# Revit family: PRD_AR_PprTwlDspnsrs_STRATOSPaperTowelDispenser_STRX637_STRX635B
name_source: partatom
category: Specialty Equipment
revit_build: Autodesk Revit 2018 (Build: 20190510_1515(x64)
units: mm (PartAtom-declared; Revit-internal decimal feet)

## family parameters
Cut with Voids When Loaded = No
Host = Face
OmniClass Number = 23.40.20.21.17
OmniClass Title = Paper Towel Dispensers, Disposal Units
Part Type = Normal
Room Calculation Point = No
Round Connector Dimension = Use Diameter
Shared = No

## types (2) — shared parameters
AssetType = Fixed
Category = Pr_40_70_22_62, Paper Towel Dispensers
Default Elevation = 900 mm  [stored 2.95276 ft]
DispenserMaterial = PRD_AR_StainlessSteel_SatinFinished
DurationUnit = year
Features = stainless steel, surface satin finished
FillingQuantity = 1
FillingQuantityUom = Rolls
Finish = satin finished
IfcExportAs = IfcFurnitureType
IfcExportType = USERDEFINED
IntegralAccessories = incl. stainless steel screws and dowels
IsBuiltIn = TRUE
Lock = Key-lock
MainColor = stainless steel
Manufacturer = KWC Group AG
ManufacturerName = KWC Group AG
ManufacturerURL = www.kwc.com
Material = stainless steel
MaterialCode = 1.4301
MaterialThickness = 1.50 mm
NBSDescription = Paper towel dispensers
NBSReference = 45-35-72/344
ProductInformation = https://pim.kwc.com
Style = dispenser
SurfaceTreatment = InoxPlus (anti fingerprint)
TypeOfConsumable = Paper roll
TypeOfFixing = Screw
TypeOfMounting = Wall mounting
TypeOfOperation = Manual operation
URL = www.kwc.com
Uniclass2015Code = Pr_40_70_22_62
Uniclass2015Title = Paper towel dispensers
Uniclass2015Version = Products v1.10
Version = 1
WarrantyDurationUnit = year

## per-type parameters (varying)
| type | BIMObjectName | Description | GrossWeight | MaximumDepthDiameterOfConsumable | MaximumWidthOfConsumable | ModelNumber | Name | NetWeight | NominalDepth | NominalHeight | NominalWidth | Size |
| STRX637 | PRD_AR_PaperTowelDispensers_STRATOSPaperTowelDispenser_STRX637 | Manual paper towel dispenser for wall mounting, stainless steel, surface satin finished, front with InoxPlus surface refinement for the reduction of finger marks and better cleaning characteristics (easy to clean), material thickness 1.5 mm, curved front with inspection window, cylinder lock with KWC standard key, capacity 1 paper roll, paper comes automatically out to pull with hand, maintenance free mechanic, electrical connection or batteries are not required, easypaper roll change mechanism, for rolls with max. width 205 mm and max. diameter 200 mm, paper length is not adjustable - one length 260 mm, includes stainless steel screws and dowels. | 7.77 kg | 200.00 mm | 205.00 mm | 2000110533 | Paper Towel Dispenser STRX637 | 7.16 kg | 227 mm  [stored 0.744751 ft] | 385 mm  [stored 1.26312 ft] | 294 mm  [stored 0.964567 ft] | 294 x 385 x 227 mm |
| STRX635B | PRD_AR_PaperTowelDispensers_STRATOSPaperTowelDispenser_STRX635B | Centerfeed paper roll box for wall mounting, stainless steel, surface satin finished, front with InoxPlus surface refinement for the reduction of finger marks and better cleaning characteristics (easy to clean), material thickness 1.5 mm, curved front cover, cylinder lock with KWC standard key, for paper rolls with max. Ø 190 mm and max. height of 250 mm, only for centerfeed paper rolls, integrated w/ stainless steel tear- off edge and strain relief avoiding paper tear-off within casing, includes stainless steel screws and dowels. | 5.32 kg | 190.00 mm | 250.00 mm | 2030025051 | Paper Towel Dispenser STRX635B | 4.70 kg | 240 mm  [stored 0.787402 ft] | 343 mm  [stored 1.12533 ft] | 205 mm  [stored 0.672572 ft] | 205 x 343 x 240 mm |

note: column(s) folded — value = type name in every type: Model, ModelReference, Type

note: [stored X ft] marks values corroborated as IEEE doubles in the binary element streams (Revit-internal decimal feet)

## geometry (parser evidence)
native form markers: Sweep x9
no freeform markers — native parametric forms only
